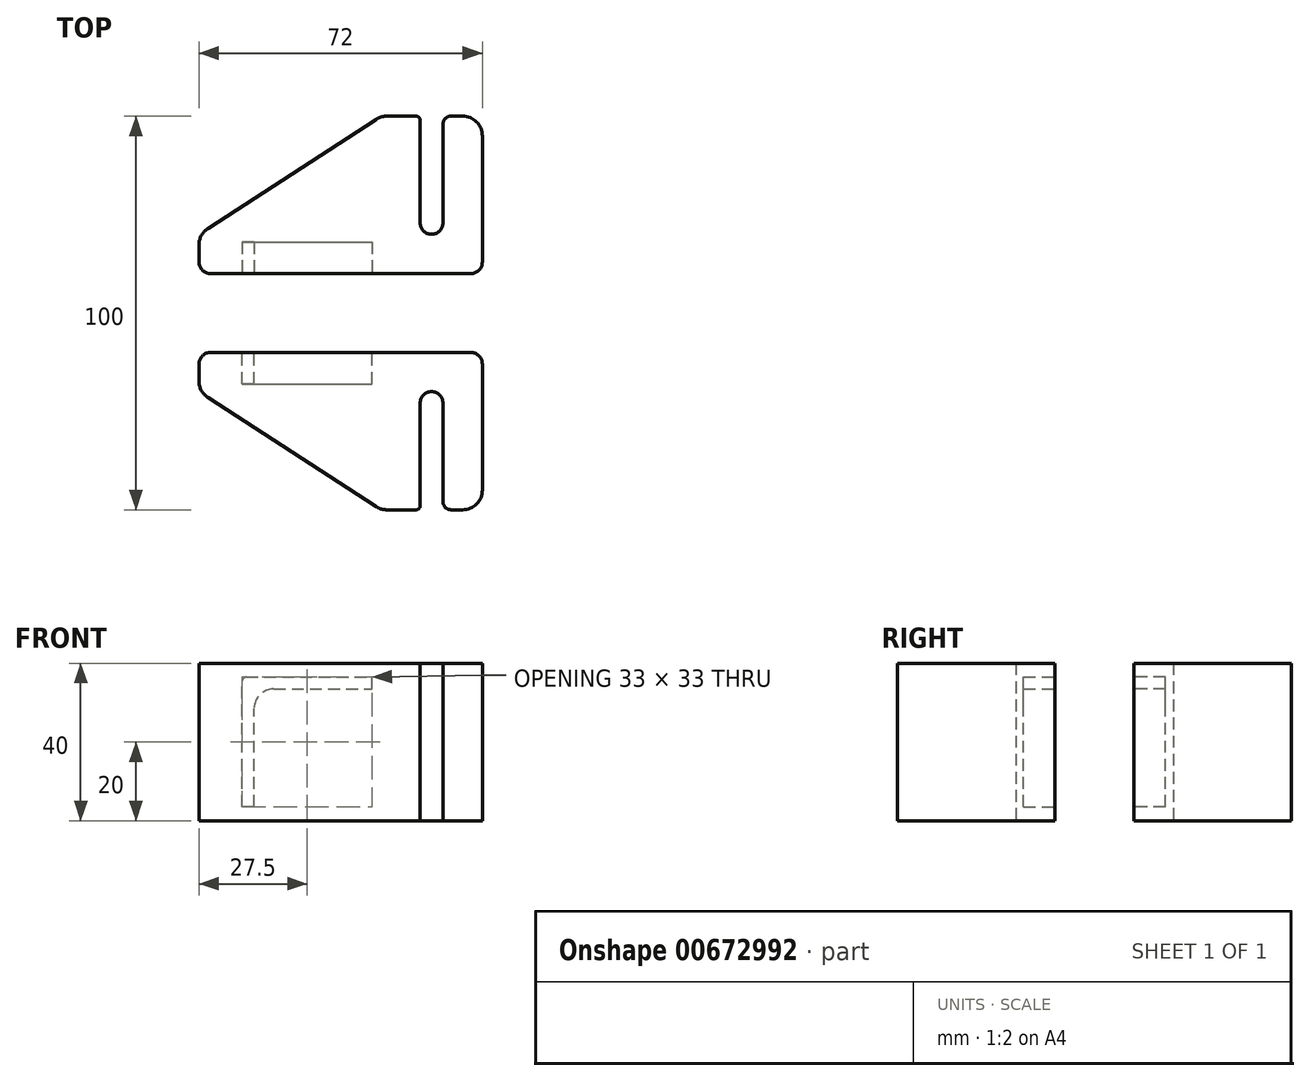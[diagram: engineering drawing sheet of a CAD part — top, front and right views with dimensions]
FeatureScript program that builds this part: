
annotation { "Feature Type Name" : "Feature", "Feature Type Description" : "" }
export const myFeature = defineFeature(function(context is Context, id is Id, definition is map)
    precondition{}
    {
        {
            var Q0;
            Q0=qCreatedBy(makeId("Top.planeOp"),FACE);
            var sketch = newSketch(context, id + "F0", { "sketchPlane" : qUnion([Q0])});
            skLineSegment(sketch, "E0.bottom", {"start": v(31, -20) * mm, "end": v(28, -20) * mm});
            skLineSegment(sketch, "E0.top", {"start": v(33, 20) * mm, "end": v(-33, 20) * mm});
            skLineSegment(sketch, "E0.left", {"start": v(36, -15) * mm, "end": v(36, 17) * mm});
            skLineSegment(sketch, "E0.right", {"start": v(-36, 12.71) * mm, "end": v(-36, 17) * mm});
            skPoint(sketch, "E0.middle", {"position": v(0, 0) * mm});
            skLineSegment(sketch, "E1.top", {"start": v(23.1, 10) * mm, "end": v(23.1, 10) * mm});
            skLineSegment(sketch, "E1.left", {"start": v(26, -18) * mm, "end": v(26, 7.1) * mm});
            skLineSegment(sketch, "E1.right", {"start": v(20.2, -19) * mm, "end": v(20.2, 7.1) * mm});
            skLineSegment(sketch, "E2.trimOffspring", {"start": v(19.2, -20) * mm, "end": v(11.68, -20) * mm});
            skLineSegment(sketch, "E3", {"start": v(8.96, -19.2) * mm, "end": v(-33.72, 8.52) * mm});
            skPoint(sketch, "E4.orphan", {"position": v(-36, -20) * mm});
            skPoint(sketch, "E5.visualSharp", {"position": v(-36, 20) * mm});
            skArc(sketch, "E5.filletArc", {"start": v(-33, 20) * mm, "mid": v(-35.12, 19.12) * mm, "end": v(-36, 17) * mm});
            skPoint(sketch, "E6.visualSharp", {"position": v(-36, 10) * mm});
            skArc(sketch, "E6.filletArc", {"start": v(-36, 12.71) * mm, "mid": v(-35.4, 10.33) * mm, "end": v(-33.72, 8.52) * mm});
            skPoint(sketch, "E7.visualSharp", {"position": v(10.2, -20) * mm});
            skArc(sketch, "E7.filletArc", {"start": v(8.96, -19.2) * mm, "mid": v(10.26, -19.8) * mm, "end": v(11.68, -20) * mm});
            skPoint(sketch, "E8.visualSharp", {"position": v(36, -20) * mm});
            skArc(sketch, "E8.filletArc", {"start": v(31, -20) * mm, "mid": v(34.54, -18.54) * mm, "end": v(36, -15) * mm});
            skPoint(sketch, "E9.visualSharp", {"position": v(36, 20) * mm});
            skArc(sketch, "E9.filletArc", {"start": v(36, 17) * mm, "mid": v(35.12, 19.12) * mm, "end": v(33, 20) * mm});
            skPoint(sketch, "E10.visualSharp", {"position": v(20.2, -20) * mm});
            skArc(sketch, "E10.filletArc", {"start": v(19.2, -20) * mm, "mid": v(19.9, -19.7) * mm, "end": v(20.2, -19) * mm});
            skPoint(sketch, "E11.visualSharp", {"position": v(26, -20) * mm});
            skArc(sketch, "E11.filletArc", {"start": v(26, -18) * mm, "mid": v(26.59, -19.41) * mm, "end": v(28, -20) * mm});
            skPoint(sketch, "E12.visualSharp", {"position": v(20.2, 10) * mm});
            skArc(sketch, "E12.filletArc", {"start": v(23.1, 10) * mm, "mid": v(21.05, 9.15) * mm, "end": v(20.2, 7.1) * mm});
            skPoint(sketch, "E13.visualSharp", {"position": v(26, 10) * mm});
            skArc(sketch, "E13.filletArc", {"start": v(26, 7.1) * mm, "mid": v(25.15, 9.15) * mm, "end": v(23.1, 10) * mm});
            skSolve(sketch);
        }
        {
            var Q0;
            Q0=makeQuery(id+"F0.imprint","IMPRINT",FACE,{"disambiguationData":[TD([[makeQuery(id+"F0.imprint","IMPRINT",EDGE,{"derivedFrom":sQuery(id+"F0.wireOp",EDGE,"E0.bottom")}),-1.0]])]});
            extrude(context, id + "F1", {"entities" : qUnion([Q0]), "endBound" : BoundingType.SYMMETRIC, "depth" : 40 * mm, "offsetDistance" : 25 * mm});
        }
        {
            var Q0;
            Q0=makeQuery(id+"F1.opExtrude","SWEPT_FACE",FACE,{"disambiguationData":[OSD([sQuery(id+"F0.wireOp",EDGE,"E0.top")])]});
            var sketch = newSketch(context, id + "F2", { "sketchPlane" : qUnion([Q0])});
            skLineSegment(sketch, "E14", {"start": v(25, -16.5) * mm, "end": v(25, 15.5) * mm});
            skLineSegment(sketch, "E15", {"start": v(24, 16.5) * mm, "end": v(-8, 16.5) * mm});
            skLineSegment(sketch, "E16.0", {"start": v(17, 13.5) * mm, "end": v(-8, 13.5) * mm});
            skLineSegment(sketch, "E16.1", {"start": v(22, -16.5) * mm, "end": v(22, 8.5) * mm});
            skLineSegment(sketch, "E17", {"start": v(22, -16.5) * mm, "end": v(25, -16.5) * mm});
            skLineSegment(sketch, "E18", {"start": v(-8, 13.5) * mm, "end": v(-8, 16.5) * mm});
            skPoint(sketch, "E19.visualSharp", {"position": v(25, 16.5) * mm});
            skArc(sketch, "E19.filletArc", {"start": v(25, 15.5) * mm, "mid": v(24.7, 16.2) * mm, "end": v(24, 16.5) * mm});
            skPoint(sketch, "E20.visualSharp", {"position": v(22, 13.5) * mm});
            skArc(sketch, "E20.filletArc", {"start": v(22, 8.5) * mm, "mid": v(20.54, 12.04) * mm, "end": v(17, 13.5) * mm});
            skLineSegment(sketch, "E21", {"start": v(-58, -32) * mm, "end": v(82, -32) * mm, "construction": true});
            skSolve(sketch);
        }
        {
            var Q0;
            Q0=makeQuery(id+"F2.imprint","IMPRINT",FACE,{"disambiguationData":[TD([[makeQuery(id+"F2.imprint","IMPRINT",EDGE,{"derivedFrom":sQuery(id+"F2.wireOp",EDGE,"E14")}),1.0]])]});
            extrude(context, id + "F3", {"entities" : qUnion([Q0]), "operationType" : NewBodyOperationType.REMOVE, "oppositeDirection" : true, "depth" : 8 * mm, "offsetDistance" : 25 * mm});
        }
        {
            var Q0;
            Q0=makeQuery(id+"F2.imprint","IMPRINT",FACE,{"disambiguationData":[TD([[makeQuery(id+"F2.imprint","IMPRINT",EDGE,{"derivedFrom":sQuery(id+"F2.wireOp",EDGE,"E14")}),-1.0]])]});
            cPlane(context, id + "F4", {"entities" : qUnion([Q0]), "cplaneType" : CPlaneType.OFFSET, "offset" : 10 * mm, "width" : 150 * mm, "height" : 150 * mm});
        }
        {
            var Q0;
            Q0=makeQuery(id+"F1.opExtrude","SWEPT_BODY",BODY,{"disambiguationData":[OSD([sQuery(id+"F0.wireOp",EDGE,"E0.bottom"),sQuery(id+"F0.wireOp",EDGE,"E0.top"),sQuery(id+"F0.wireOp",EDGE,"E0.left"),sQuery(id+"F0.wireOp",EDGE,"E0.right"),sQuery(id+"F0.wireOp",EDGE,"E1.left"),sQuery(id+"F0.wireOp",EDGE,"E1.right"),sQuery(id+"F0.wireOp",EDGE,"E2.trimOffspring"),sQuery(id+"F0.wireOp",EDGE,"E3"),sQuery(id+"F0.wireOp",EDGE,"E5.filletArc"),sQuery(id+"F0.wireOp",EDGE,"E6.filletArc"),sQuery(id+"F0.wireOp",EDGE,"E7.filletArc"),sQuery(id+"F0.wireOp",EDGE,"E8.filletArc"),sQuery(id+"F0.wireOp",EDGE,"E9.filletArc"),sQuery(id+"F0.wireOp",EDGE,"E10.filletArc"),sQuery(id+"F0.wireOp",EDGE,"E11.filletArc"),sQuery(id+"F0.wireOp",EDGE,"E12.filletArc"),sQuery(id+"F0.wireOp",EDGE,"E13.filletArc")])]});
            var Q1;
            Q1=qCreatedBy(id+"F4.planeOp",FACE);
            mirror(context, id + "F5", {"entities" : qUnion([Q0]), "mirrorPlane" : qUnion([Q1])});
        }
    });
